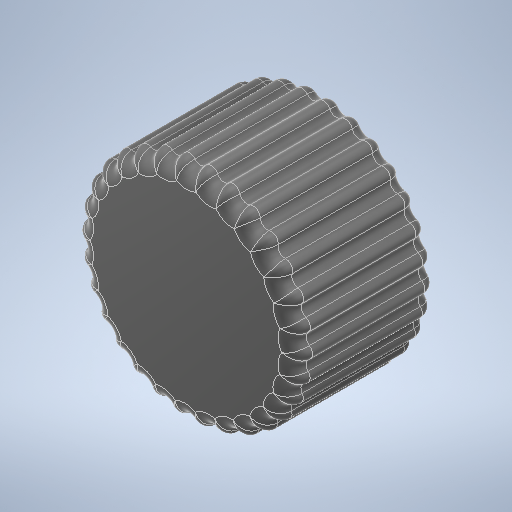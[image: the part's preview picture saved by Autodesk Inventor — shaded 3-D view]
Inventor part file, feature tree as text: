
AUTODESK INVENTOR PART (.ipt)
format: ipt  version: 2025.1 (Build 291241020, 241B)  size: 2,321,920 bytes
history: native  units: mm
features: fillet x2, sketch x2, revolve x1, extrude x1, pattern_circular x1
ambient origin geometry x8: Origin, YZ Plane, XZ Plane, XY Plane, X Axis, Y Axis, Z Axis, Center Point
bodies: Solid1 (feature_tree)
feature tree (7):
  revolve  "Revolution1"  [1 undecoded]
  extrude  "Extrusion1"  Depth=5.0mm
  fillet  "Fillet1"  [1 undecoded]
  pattern_circular  "Circular Pattern1"  [2 undecoded]
  fillet  "Fillet2"  Radius=14.0mm
  sketch  "Sketch1"  dims[d0=16.15mm d1=10.2mm]
  sketch  "Sketch2"  dims[d2=20.0mm d3=5.0mm d4=360.0deg d5=1.2mm d6=14.0mm d7=16.5mm d8=0.0mm d9=0.0mm d10=1.0mm d11=300.0mm d12=360.0deg d14=2.0mm]
note: 4 required parameter values undecoded (feature->parameter linkage not recoverable at this tier; creation-order binding heuristic only, values carry confidence <= 0.55)